# Revit family: PLFX_Wall Mounted Toilet
name_source: partatom
category: Plumbing Fixtures
revit_build: Autodesk Revit Architecture 2012 (Build: 20110622_0930(x64)
units: mm (PartAtom-declared; Revit-internal decimal feet)

## types (1)
- PLFX_Wall Mounted Toilet
    ADA Compliant = Yes
    Assembly Code = D2010100
    CADworks URL = http://www.CADworks.net
    CW Connection = Yes
    CWFU = 0
    Cold Water Connection NPT = 1"
    Cold Water Connection Radius = 0' - 0 1/2"
    Default Elevation = 1' - 3"
    Description = Wall Hung Flushometer Toilet
    Flush Valve Model = TET1LN32
    Gallons Per Flush = 1.28
    HW Connection = Yes
    HWFU = 0
    Manufacturer = TOTO
    Model = CT708E
    Nominal Height = 1' - 0 3/4"
    Nominal Length = 2' - 0 7/8"
    Nominal Width = 1' - 3 3/4"
    Product URL = http://www.totousa.com
    Shipping Weight = 49.00 lb
    Supply Height from Floor = 2' - 2 1/2"
    Supply Offset from Center = 0' - 4 3/4"
    URL = http://www.totousa.com
    Vent Connection = Yes
    WFU = 0
    Wall Closure Offset = 0' - 2 3/4"
    Waste Connection = Yes
    Waste Connection NPT = 4"
    Waste Height Offset = 0' - 5 3/8"
    Water Closet Material = <By Category>

## geometry (parser evidence)
native form markers: Sweep x2
no freeform markers — native parametric forms only
